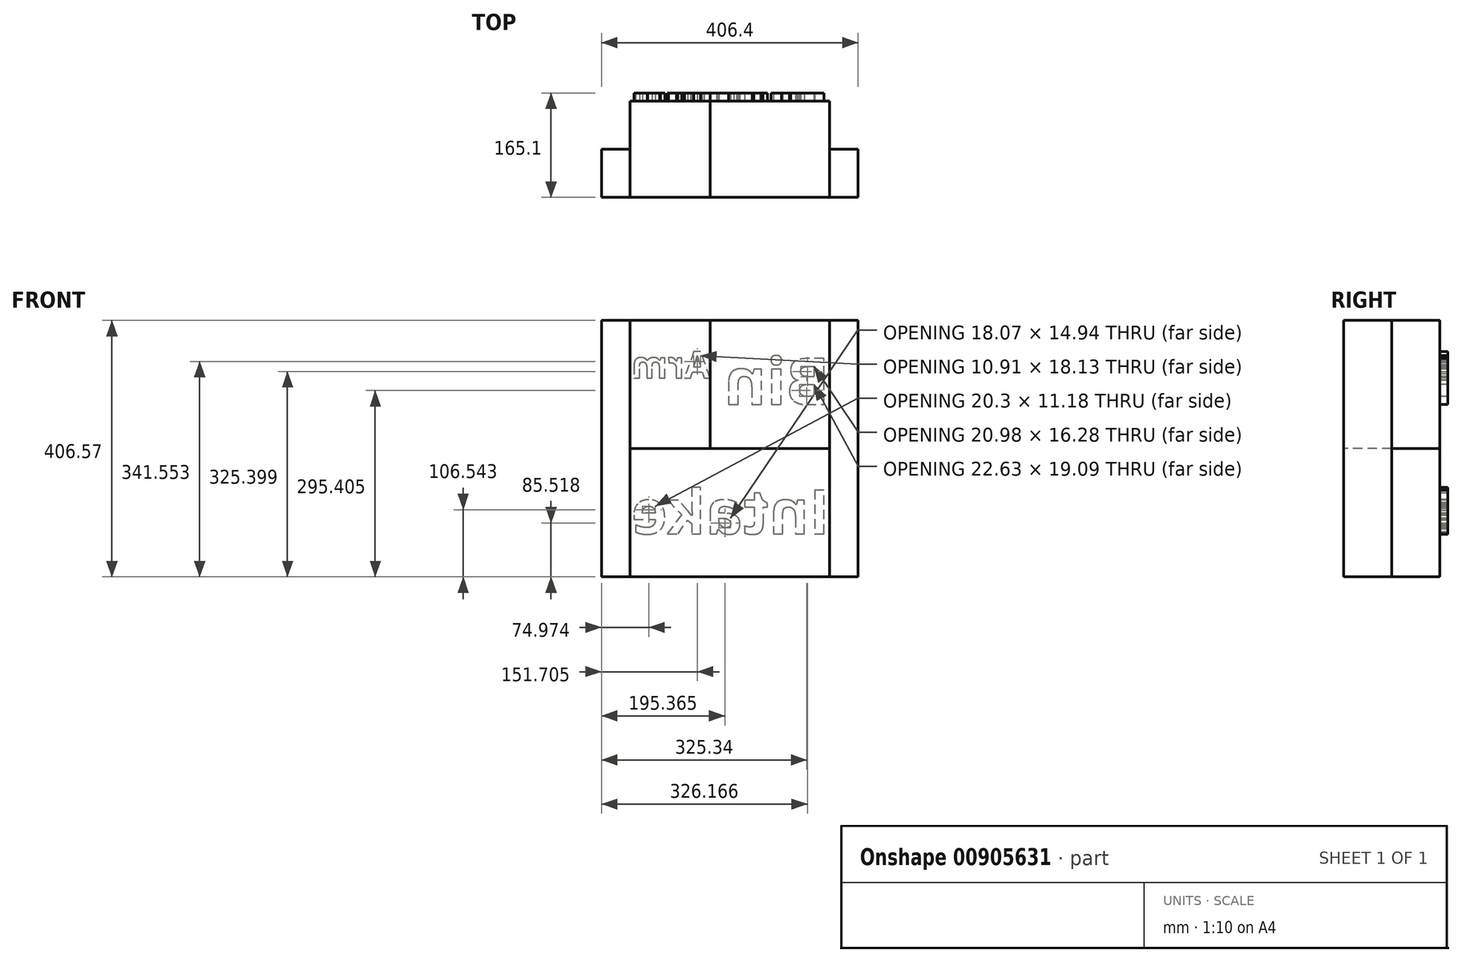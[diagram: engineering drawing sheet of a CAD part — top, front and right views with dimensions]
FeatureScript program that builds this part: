
annotation { "Feature Type Name" : "Feature", "Feature Type Description" : "" }
export const myFeature = defineFeature(function(context is Context, id is Id, definition is map)
    precondition{}
    {
        {
            var Q0;
            Q0=qCreatedBy(makeId("Front.planeOp"),FACE);
            var sketch = newSketch(context, id + "F0", { "sketchPlane" : qUnion([Q0])});
            skPoint(sketch, "E0.middle", {"position": v(-203.16, 0) * mm});
            skLineSegment(sketch, "E1.bottom", {"start": v(135.74, 203.2) * mm, "end": v(180.74, 203.2) * mm});
            skLineSegment(sketch, "E1.top", {"start": v(135.74, -203.2) * mm, "end": v(180.74, -203.2) * mm});
            skLineSegment(sketch, "E1.left", {"start": v(135.74, 203.2) * mm, "end": v(135.74, -203.2) * mm});
            skLineSegment(sketch, "E1.right", {"start": v(180.74, 203.2) * mm, "end": v(180.74, -203.2) * mm});
            skPoint(sketch, "E1.middle", {"position": v(158.24, 0) * mm});
            skLineSegment(sketch, "E2.bottom", {"start": v(-180.66, 203.2) * mm, "end": v(-53.66, 203.2) * mm});
            skLineSegment(sketch, "E2.top", {"start": v(-180.66, 0) * mm, "end": v(-53.66, 0) * mm});
            skLineSegment(sketch, "E2.left", {"start": v(-180.66, 203.2) * mm, "end": v(-180.66, 0) * mm});
            skLineSegment(sketch, "E2.right", {"start": v(-53.66, 203.2) * mm, "end": v(-53.66, 0) * mm});
            skLineSegment(sketch, "E3.bottom", {"start": v(135.74, 203.2) * mm, "end": v(-53.66, 203.2) * mm});
            skLineSegment(sketch, "E3.top", {"start": v(135.74, 0) * mm, "end": v(-53.66, 0) * mm});
            skLineSegment(sketch, "E3.left", {"start": v(135.74, 203.2) * mm, "end": v(135.74, 0) * mm});
            skLineSegment(sketch, "E4.bottom", {"start": v(-180.66, 0) * mm, "end": v(135.74, 0) * mm});
            skLineSegment(sketch, "E4.top", {"start": v(-180.66, -203.2) * mm, "end": v(135.74, -203.2) * mm});
            skLineSegment(sketch, "E4.left", {"start": v(-180.66, 0) * mm, "end": v(-180.66, -203.2) * mm});
            skLineSegment(sketch, "E4.right", {"start": v(135.74, 0) * mm, "end": v(135.74, -203.2) * mm});
            skSolve(sketch);
        }
        {
            var Q0;
            Q0=makeQuery(id+"F0.imprint","IMPRINT",FACE,{"disambiguationData":[TD([[makeQuery(id+"F0.imprint","IMPRINT",EDGE,{"derivedFrom":sQuery(id+"F0.wireOp",EDGE,"E2.bottom")}),-1.0]])]});
            var sketch = newSketch(context, id + "F1", { "sketchPlane" : qUnion([Q0])});
            skLineSegment(sketch, "E5.bottom", {"start": v(-180.66, 203.37) * mm, "end": v(-225.66, 203.37) * mm});
            skLineSegment(sketch, "E5.top", {"start": v(-180.66, -203.03) * mm, "end": v(-225.66, -203.03) * mm});
            skLineSegment(sketch, "E5.left", {"start": v(-180.66, 203.37) * mm, "end": v(-180.66, -203.03) * mm});
            skLineSegment(sketch, "E5.right", {"start": v(-225.66, 203.37) * mm, "end": v(-225.66, -203.03) * mm});
            skSolve(sketch);
        }
        {
            var Q0;
            {var subQ4=sQuery(id+"F1.wireOp",EDGE,"E5.bottom");Q0=makeQuery(id+"F1.imprint","IMPRINT",FACE,{"disambiguationData":[TD([[makeQuery(id+"F1.imprint","IMPRINT",EDGE,{"derivedFrom":subQ4}),1.0]])]});}
            extrude(context, id + "F2", {"entities" : qUnion([Q0]), "depth" : -76.2 * mm, "offsetDistance" : 25.4 * mm});
        }
        {
            var Q0;
            Q0=makeQuery(id+"F0.imprint","IMPRINT",FACE,{"disambiguationData":[TD([[makeQuery(id+"F0.imprint","IMPRINT",EDGE,{"derivedFrom":sQuery(id+"F0.wireOp",EDGE,"E1.bottom")}),-1.0]])]});
            extrude(context, id + "F3", {"entities" : qUnion([Q0]), "depth" : -76.2 * mm, "offsetDistance" : 25.4 * mm});
        }
        {
            var Q0;
            Q0=makeQuery(id+"F0.imprint","IMPRINT",FACE,{"disambiguationData":[TD([[makeQuery(id+"F0.imprint","IMPRINT",EDGE,{"derivedFrom":sQuery(id+"F0.wireOp",EDGE,"E4.top")}),1.0]])]});
            extrude(context, id + "F4", {"entities" : qUnion([Q0]), "depth" : -152.4 * mm, "offsetDistance" : 25.4 * mm});
        }
        {
            var Q0;
            Q0=makeQuery(id+"F0.imprint","IMPRINT",FACE,{"disambiguationData":[TD([[makeQuery(id+"F0.imprint","IMPRINT",EDGE,{"derivedFrom":sQuery(id+"F0.wireOp",EDGE,"E3.bottom")}),1.0]])]});
            extrude(context, id + "F5", {"entities" : qUnion([Q0]), "depth" : -152.4 * mm, "offsetDistance" : 25.4 * mm});
        }
        {
            var Q0;
            Q0=makeQuery(id+"F0.imprint","IMPRINT",FACE,{"disambiguationData":[TD([[makeQuery(id+"F0.imprint","IMPRINT",EDGE,{"derivedFrom":sQuery(id+"F0.wireOp",EDGE,"E2.bottom")}),-1.0]])]});
            extrude(context, id + "F6", {"entities" : qUnion([Q0]), "depth" : -152.4 * mm, "offsetDistance" : 25.4 * mm});
        }
        {
            var Q0;
            Q0=makeQuery(id+"F5.opExtrude","CAP_FACE",FACE,{"disambiguationData":[OSD([sQuery(id+"F0.wireOp",EDGE,"E3.bottom"),sQuery(id+"F0.wireOp",EDGE,"E3.left"),sQuery(id+"F0.wireOp",EDGE,"E2.right"),sQuery(id+"F0.wireOp",EDGE,"E4.bottom")])],"isStart":false});
            var sketch = newSketch(context, id + "F7", { "sketchPlane" : qUnion([Q0])});
            skText(sketch, "E6", { "text": "Bin", "fontName": "OpenSans-Bold.ttf"});
            skText(sketch, "E7", { "text": "Arm", "fontName": "OpenSans-Bold.ttf"});
            const initialGuessF7  = {"E6": [-0.13574, 0.06984, 1, 0, 0.07385], "E7": [0.05366, 0.11187, 1, 0, 0.04224]};
            skSetInitialGuess(sketch, initialGuessF7);
            skSolve(sketch);
        }
        {
            var Q0;
            Q0=makeQuery(id+"F4.opExtrude","CAP_FACE",FACE,{"disambiguationData":[OSD([sQuery(id+"F0.wireOp",EDGE,"E4.bottom"),sQuery(id+"F0.wireOp",EDGE,"E4.top"),sQuery(id+"F0.wireOp",EDGE,"E4.left"),sQuery(id+"F0.wireOp",EDGE,"E4.right")])],"isStart":false});
            var sketch = newSketch(context, id + "F8", { "sketchPlane" : qUnion([Q0])});
            skText(sketch, "E8", { "text": "Intake\n", "fontName": "OpenSans-Bold.ttf"});
            const initialGuessF8  = {"E8": [-0.13574, -0.13477, 1, 0, 0.0699]};
            skSetInitialGuess(sketch, initialGuessF8);
            skSolve(sketch);
        }
        {
            var Q0;
            Q0 = qSketchRegion(id + "F7", true);
            var Q1;
            Q1 = qSketchRegion(id + "F8", true);
            extrude(context, id + "F9", {"entities" : qUnion([Q0, Q1]), "depth" : 12.7 * mm, "offsetDistance" : 25.4 * mm});
        }
    });
